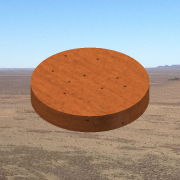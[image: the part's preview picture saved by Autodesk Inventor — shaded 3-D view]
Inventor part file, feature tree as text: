
AUTODESK INVENTOR PART (.ipt)
format: ipt  version: 2014 SP1 (Build 180222100, 222)  size: 126,464 bytes
history: native  units: in
note: dims shown in document units (in); Inventor stores cm internally (conversion verified against a paired STEP export)
features: extrude x1, sketch x1
ambient origin geometry x8: Origin, YZ Plane, XZ Plane, XY Plane, X Axis, Y Axis, Z Axis, Center Point
bodies: Solid1 (feature_tree)
feature tree (2):
  extrude  "Extrusion1"  Depth=0.5in TaperAngle=0.0deg
  sketch  "Sketch1"  dims[d0=3.0in d1=0.5in d2=0.0in]
